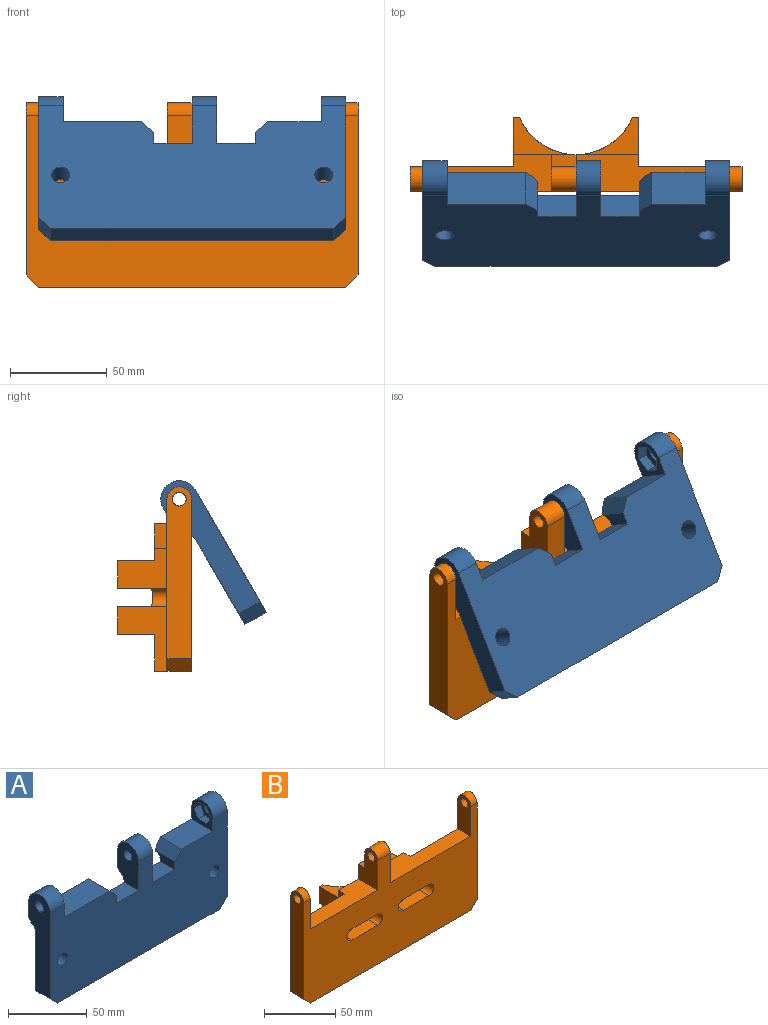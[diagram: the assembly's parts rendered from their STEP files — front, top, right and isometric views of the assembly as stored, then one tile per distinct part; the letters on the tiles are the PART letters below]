
ASSEMBLY  parts=2 mates=1
PART A: 57 faces, bbox 158.8x19.1x82.6 mm
  f0: plane 40.51x19.05mm, normal (0,0,1), area 771.8mm2, adj f3,f10,f11,f56
  f1: plane 13.24x12.7mm, normal (0,1,0), area 168.2mm2, adj f6,f16,f22,f24
  f2: plane 44.23x13.24mm, normal (0,1,0), area 278.6mm2, adj f7,f17,f18,f21,f23,f55
  f3: plane 158.75x73.03mm, normal (0,-1,0), area 9725.4mm2, adj f0,f10,f12,f13,f14,f16,f17,f18
  f4: cylinder r=6.35mm len=12.7mm, axis (1,0,0), area 99.3mm2, adj f6,f22,f24,f32
  f5: cylinder r=6.35mm len=46.86mm, axis (1,0,0), area 366.3mm2, adj f7,f18,f32,f52
  f6: plane 12.7x2.99mm, normal (0,0.82,-0.58), area 46.6mm2, adj f1,f4,f22,f24
  f7: plane 46.86x2.99mm, normal (0,0.82,-0.58), area 167.6mm2, adj f2,f5,f18,f52,f55
  f8: cylinder r=3.57mm len=7.14mm, axis (1,0,0), area 160.2mm2, adj f24,f46
  f9: cylinder r=3.57mm len=7.14mm, axis (1,0,0), area 160.2mm2, adj f19,f33
  f10: plane 19.05x19.05mm, normal (1,0,0), area 178.6mm2, adj f0,f3,f11,f20,f34,f35,f36,f37
  f11: plane 56.93x13.24mm, normal (0,1,0), area 325.8mm2, adj f0,f10,f19,f20,f50,f56
  f12: plane 146.05x12.7mm, normal (0,0,-1), area 1854.8mm2, adj f3,f32,f47,f48
  f13: cylinder r=4.62mm len=12.7mm, axis (0,-1,0), area 368.9mm2, adj f3,f32
  f14: cylinder r=4.62mm len=12.7mm, axis (0,-1,0), area 368.9mm2, adj f3,f32
  f15: cylinder r=3.57mm len=7.14mm, axis (1,0,0), area 160.2mm2, adj f18,f25
  f16: cylinder r=9.53mm len=19.05mm, axis (1,0,0), area 380mm2, adj f1,f3,f22,f24
  f17: cylinder r=9.53mm len=19.05mm, axis (1,0,0), area 380mm2, adj f2,f3,f18,f23
  f18: plane 76.2x19.05mm, normal (1,0,0), area 1056.1mm2, adj f2,f3,f5,f7,f15,f17,f32,f47
  f19: plane 76.2x19.05mm, normal (-1,0,0), area 1056.1mm2, adj f3,f9,f11,f20,f32,f48,f49,f50
  f20: cylinder r=9.53mm len=19.05mm, axis (1,0,0), area 380mm2, adj f3,f10,f11,f19
  f21: plane 27.81x19.05mm, normal (0,0,1), area 529.8mm2, adj f2,f3,f23,f55
  f22: plane 31.75x19.05mm, normal (1,0,0), area 386.3mm2, adj f1,f3,f4,f6,f16,f40,f41,f42
  f23: plane 19.05x19.05mm, normal (-1,0,0), area 178.6mm2, adj f2,f3,f17,f21,f26,f27,f28,f29
  f24: plane 31.75x19.05mm, normal (-1,0,0), area 491.6mm2, adj f1,f3,f4,f6,f8,f16,f53
  f25: plane 14.96x12.95mm, normal (-1,0,0), area 105.3mm2, adj f15,f26,f27,f28,f29,f30,f31
  f26: plane 6.48x5.56mm, normal (0,-0.87,0.5), area 41.6mm2, adj f23,f25,f27,f31
  f27: plane 7.48x5.56mm, normal (0,0,1), area 41.6mm2, adj f23,f25,f26,f28
  f28: plane 6.48x5.56mm, normal (0,0.87,0.5), area 41.6mm2, adj f23,f25,f27,f29
  f29: plane 6.48x5.56mm, normal (0,0.87,-0.5), area 41.6mm2, adj f23,f25,f28,f30
  f30: plane 7.48x5.56mm, normal (0,0,-1), area 41.6mm2, adj f23,f25,f29,f31
  f31: plane 6.48x5.56mm, normal (0,-0.87,-0.5), area 41.6mm2, adj f23,f25,f26,f30
  f32: plane 158.75x50.8mm, normal (0,1,0), area 7889.9mm2, adj f4,f5,f12,f13,f14,f18,f19,f47
  f33: plane 14.96x12.95mm, normal (1,0,0), area 105.3mm2, adj f9,f34,f35,f36,f37,f38,f39
  f34: plane 6.48x5.56mm, normal (0,-0.87,0.5), area 41.6mm2, adj f10,f33,f35,f39
  f35: plane 6.48x5.56mm, normal (0,-0.87,-0.5), area 41.6mm2, adj f10,f33,f34,f36
  f36: plane 7.48x5.56mm, normal (0,0,-1), area 41.6mm2, adj f10,f33,f35,f37
  f37: plane 6.48x5.56mm, normal (0,0.87,-0.5), area 41.6mm2, adj f10,f33,f36,f38
  f38: plane 6.48x5.56mm, normal (0,0.87,0.5), area 41.6mm2, adj f10,f33,f37,f39
  f39: plane 7.48x5.56mm, normal (0,0,1), area 41.6mm2, adj f10,f33,f34,f38
  f40: plane 6.48x5.56mm, normal (0,0.87,0.5), area 41.6mm2, adj f22,f41,f45,f46
  f41: plane 7.48x5.56mm, normal (0,0,1), area 41.6mm2, adj f22,f40,f42,f46
  f42: plane 6.48x5.56mm, normal (0,-0.87,0.5), area 41.6mm2, adj f22,f41,f43,f46
  f43: plane 6.48x5.56mm, normal (0,-0.87,-0.5), area 41.6mm2, adj f22,f42,f44,f46
  f44: plane 7.48x5.56mm, normal (0,0,-1), area 41.6mm2, adj f22,f43,f45,f46
  f45: plane 6.48x5.56mm, normal (0,0.87,-0.5), area 41.6mm2, adj f22,f40,f44,f46
  f46: plane 14.96x12.95mm, normal (1,0,0), area 105.3mm2, adj f8,f40,f41,f42,f43,f44,f45
  f47: plane 12.7x6.35mm, normal (0.71,0,-0.71), area 114mm2, adj f3,f12,f18,f32
  f48: plane 12.7x6.35mm, normal (-0.71,0,-0.71), area 114mm2, adj f3,f12,f19,f32
  f49: cylinder r=6.35mm len=59.56mm, axis (1,0,0), area 465.6mm2, adj f19,f32,f50,f54
  f50: plane 59.56x2.99mm, normal (0,0.82,-0.58), area 214.1mm2, adj f11,f19,f49,f54,f56
  f51: plane 19.81x12.7mm, normal (0,0,1), area 251.6mm2, adj f3,f22,f32,f52
  f52: plane 17.19x6.35mm, normal (-1,0,0), area 89.1mm2, adj f3,f5,f7,f51,f55
  f53: plane 19.81x12.7mm, normal (0,0,1), area 251.6mm2, adj f3,f24,f32,f54
  f54: plane 17.19x6.35mm, normal (1,0,0), area 89.1mm2, adj f3,f49,f50,f53,f56
  f55: plane 19.05x6.35mm, normal (-0.71,0,0.71), area 167.6mm2, adj f2,f3,f7,f21,f52
  f56: plane 19.05x6.35mm, normal (0.71,0,0.71), area 167.6mm2, adj f0,f3,f11,f50,f54
PART B: 45 faces, bbox 171.5x38.1x95.3 mm
  f0: plane 12.7x6.35mm, normal (0,0,1), area 80.6mm2, adj f2,f20,f38,f41
  f1: plane 171.45x88.9mm, normal (0,-1,0), area 10859.1mm2, adj f4,f5,f16,f17,f18,f26,f27,f28
  f2: plane 12.7x12.7mm, normal (0,1,0), area 161.3mm2, adj f0,f4,f38,f41
  f3: plane 88.9x53.45mm, normal (0,1,0), area 3440.9mm2, adj f5,f7,f13,f16,f18,f31,f32,f33
  f4: cylinder r=6.35mm len=12.7mm, axis (-1,0,0), area 253.4mm2, adj f1,f2,f38,f41
  f5: cylinder r=6.35mm len=12.7mm, axis (-1,0,0), area 124.1mm2, adj f1,f3,f16,f37
  f6: cylinder r=3.57mm len=7.14mm, axis (-1,0,0), area 139.5mm2, adj f16,f37
  f7: plane 33.34x25.4mm, normal (1,0,0), area 483.9mm2, adj f3,f8,f18,f23,f25,f32
  f8: plane 14.29x3.18mm, normal (0,1,0), area 45.4mm2, adj f7,f10,f25,f32
  f9: plane 88.9x53.45mm, normal (0,1,0), area 3440.9mm2, adj f12,f17,f18,f19,f26,f28,f29,f34
  f10: cylinder r=31.75mm len=58.2mm, axis (0,0,1), area 2276.7mm2, adj f8,f11,f14,f15,f21,f22,f24,f25
  f11: plane 14.29x3.18mm, normal (0,1,0), area 45.4mm2, adj f10,f12,f22,f28
  f12: plane 25.4x20.64mm, normal (-1,0,0), area 403.2mm2, adj f9,f11,f20,f22,f28,f39
  f13: plane 25.4x20.64mm, normal (1,0,0), area 403.2mm2, adj f3,f14,f20,f21,f31,f36
  f14: plane 14.29x3.18mm, normal (0,1,0), area 45.4mm2, adj f10,f13,f21,f31
  f15: plane 14.29x3.18mm, normal (0,1,0), area 45.4mm2, adj f10,f19,f24,f29
  f16: plane 88.9x12.7mm, normal (1,0,0), area 1071.7mm2, adj f1,f3,f5,f6,f44
  f17: plane 88.9x12.7mm, normal (-1,0,0), area 1071.7mm2, adj f1,f9,f34,f35,f43
  f18: plane 158.75x19.05mm, normal (0,0,-1), area 2426mm2, adj f1,f3,f7,f9,f19,f23,f43,f44
  f19: plane 33.34x25.4mm, normal (-1,0,0), area 483.9mm2, adj f9,f15,f18,f23,f24,f29
  f20: plane 64.55x19.05mm, normal (0,1,0), area 571.2mm2, adj f0,f12,f13,f21,f22,f36,f38,f39
  f21: plane 32.27x19.05mm, normal (0,0,1), area 215.3mm2, adj f10,f13,f14,f20
  f22: plane 32.27x19.05mm, normal (0,0,1), area 215.3mm2, adj f10,f11,f12,f20
  f23: plane 64.55x19.05mm, normal (0,1,0), area 1229.7mm2, adj f7,f18,f19,f24,f25
  f24: plane 32.27x19.05mm, normal (0,0,-1), area 215.3mm2, adj f10,f15,f19,f23
  f25: plane 32.27x19.05mm, normal (0,0,-1), area 215.3mm2, adj f7,f8,f10,f23
  f26: cylinder r=4.76mm len=12.7mm, axis (0,-1,0), area 190mm2, adj f1,f9,f28,f29
  f27: cylinder r=4.76mm len=21.7mm, axis (0,-1,0), area 308.2mm2, adj f1,f10,f28,f29
  f28: plane 38.1x25.4mm, normal (0,0,-1), area 651.1mm2, adj f1,f9,f10,f11,f12,f26,f27
  f29: plane 38.1x25.4mm, normal (0,0,1), area 651.1mm2, adj f1,f9,f10,f15,f19,f26,f27
  f30: cylinder r=4.76mm len=21.7mm, axis (0,-1,0), area 308.2mm2, adj f1,f10,f31,f32
  f31: plane 38.1x25.4mm, normal (0,0,-1), area 651.1mm2, adj f1,f3,f10,f13,f14,f30,f33
  f32: plane 38.1x25.4mm, normal (0,0,1), area 651.1mm2, adj f1,f3,f7,f8,f10,f30,f33
  f33: cylinder r=4.76mm len=12.7mm, axis (0,-1,0), area 190mm2, adj f1,f3,f31,f32
  f34: cylinder r=6.35mm len=12.7mm, axis (-1,0,0), area 124.1mm2, adj f1,f9,f17,f40
  f35: cylinder r=3.57mm len=7.14mm, axis (-1,0,0), area 139.5mm2, adj f17,f40
  f36: plane 79.5x19.05mm, normal (0,0,1), area 1214.6mm2, adj f1,f3,f13,f20,f37,f38
  f37: plane 31.75x12.7mm, normal (-1,0,0), area 345.9mm2, adj f1,f3,f5,f6,f36
  f38: plane 31.75x19.05mm, normal (1,0,0), area 426.6mm2, adj f0,f1,f2,f4,f20,f36,f42
  f39: plane 66.8x19.05mm, normal (0,0,1), area 972.7mm2, adj f1,f9,f12,f20,f40,f41
  f40: plane 31.75x12.7mm, normal (1,0,0), area 345.9mm2, adj f1,f9,f34,f35,f39
  f41: plane 31.75x19.05mm, normal (-1,0,0), area 426.6mm2, adj f0,f1,f2,f4,f20,f39,f42
  f42: cylinder r=3.57mm len=12.7mm, axis (-1,0,0), area 284.8mm2, adj f38,f41
  f43: plane 12.7x6.35mm, normal (-0.71,0,-0.71), area 114mm2, adj f1,f9,f17,f18
  f44: plane 12.7x6.35mm, normal (0.71,0,-0.71), area 114mm2, adj f1,f3,f16,f18
PLACE A rot(axis=(-1,0,0),30.1deg) t=(31.76,15.59,34.56)mm
PLACE B t=(31.64,34.42,24.24)mm fixed
MATE cylindrical A.f8 <-> B.f4  axis (1,0,0) through (111.14,28.07,75.04)mm
